# Revit family: Lighting_Outside_Zero_Elements_Wall_Outside
name_source: partatom
category: Lighting Fixtures
revit_build: Autodesk Revit 2018 (Build: 20170223_1515(x64)
units: mm (PartAtom-declared; Revit-internal decimal feet)

## family parameters
Cut with Voids When Loaded = No
Host = Face
Light Source = Yes
OmniClass Number = 23.80.70.00
OmniClass Title = Lighting
Part Type = Normal
Room Calculation Point = No
Round Connector Dimension = Use Diameter
Shared = No

## types (2) — shared parameters
AssetType = Fixed
BIMObjectName = Lighting_Outside_Zero_Elements_Wall_Outside
BIMobject category = Outside
BIMobject category code = lighting-outside
BIMobject main category = Lighting
BIMobject main category code = lighting
Brand = Zero
Brand url = http://www.zero.se
Category = Wall
Collection = Elements
Color Filter = 16777215
Design country = Sweden
Designer = Note Design Studio
Dimming = None
Dimming Lamp Color Temperature Shift = <None>
DurationUnit = Year
Edition number = 1
Emit Shape Visible in Rendering = No
Emit from Rectangle Length = 1219 mm
Emit from Rectangle Width = 610 mm
Features = Terminal-block 5x4mm2
Finish = Silver grey (RAL 9006) painted metal or hot-dip galvanized metal. Other colours on request. Hot-dip galvanized has a ruff finish with visible scratches and other marks.
HasProtectiveEarth = Yes
IP_Code = IP65
IfcExportAs = IfcLightFixtureType
IfcExportType = NOTDEFINED
LightFixtureMountingType = Surface
LightFixturePlacingType = Wall
Manufacturer = Zero
Manufacturer country = Sweden
Manufacturer name = ZERO
ManufacturerName = Zero
ManufacturerURL = https://www.zerolighting.com
Material = Steel
Material main = Steel
NBSDescription = General purpose luminaires
NBSReference = 90-60-50/405
Name = Zero_Elements_Wall_Outside
Nominal height = 274 mm  [stored 0.89895 ft]
Nominal width = 285 mm  [stored 0.935039 ft]
NominalCurrent = 0 A
NominalFrequencyRange = 50 Hz
NominalLength = 285 mm  [stored 0.935039 ft]
NominalVoltage = 230 V
NominalVoltageCalc = 0 V
NumberOfPoles = 1
PhaseAngle = 0.00°
Photometric Web File = Elements3385.IES
Product Guid = ce742e59-943e-4774-a16b-033299cc1537
Product SKU = Elements_wall_fixture_outdoor
Product family = Elements
Product group = Wall fixture
Product url = https://www.zerolighting.com
ProductInformation = An outdoor fixture joins the Elements series. Arched surfaces of galvanised steel replace the textiles used previously, all the better to survive the seasons of the harsh Nordic climate. Via the domed material layer, light is reflected and directed to give stylistically pure illumination on the facade. Even in this material, Elements reminds us of the Nordic mountainous countryside and its very special light. IK10
QR code = http://bimobject.com
Revision = 4
Shape = Sculptured
Size = 285x274x142 mm
Tilt Angle = -90.00°
TotalWattage = 8 W
URL = https://www.zerolighting.com
Uniclass2 = Pr_70_70_49
Uniclass2015Description = Surface luminaires
Uniclass2015Reference = Pr_70_70_48_85
UsageCurrent = 0 A
Version = 2
VersionDate = 20/12/2021
WarrantyDurationUnit = Year
Weight Net (Kg) = 1.8
zero-valued in all types: Default Elevation, ElectricalDeviceNominalPower, MaintenanceFactor, NumberOfSources

## per-type parameters (varying)
| type | ArticleNumber | Color | LightFixtureMainMaterial | Model | ModelNumber |
| LED 366LM Galvanized | 3385-1-83 | Metallic | Steel, Galvanized | Elements exterior wall LED 366LM Galvanized | 3385-1-83 |
| LED 366LM Grey | 3385-1-10 | Grey | Silver Grey Metal RAL 9006 | Elements exterior wall LED 366LM Silver Grey | 3385-1-10 |

note: [stored X ft] marks values corroborated as IEEE doubles in the binary element streams (Revit-internal decimal feet)

## geometry (parser evidence)
native form markers: Sweep x4
no freeform markers — native parametric forms only
